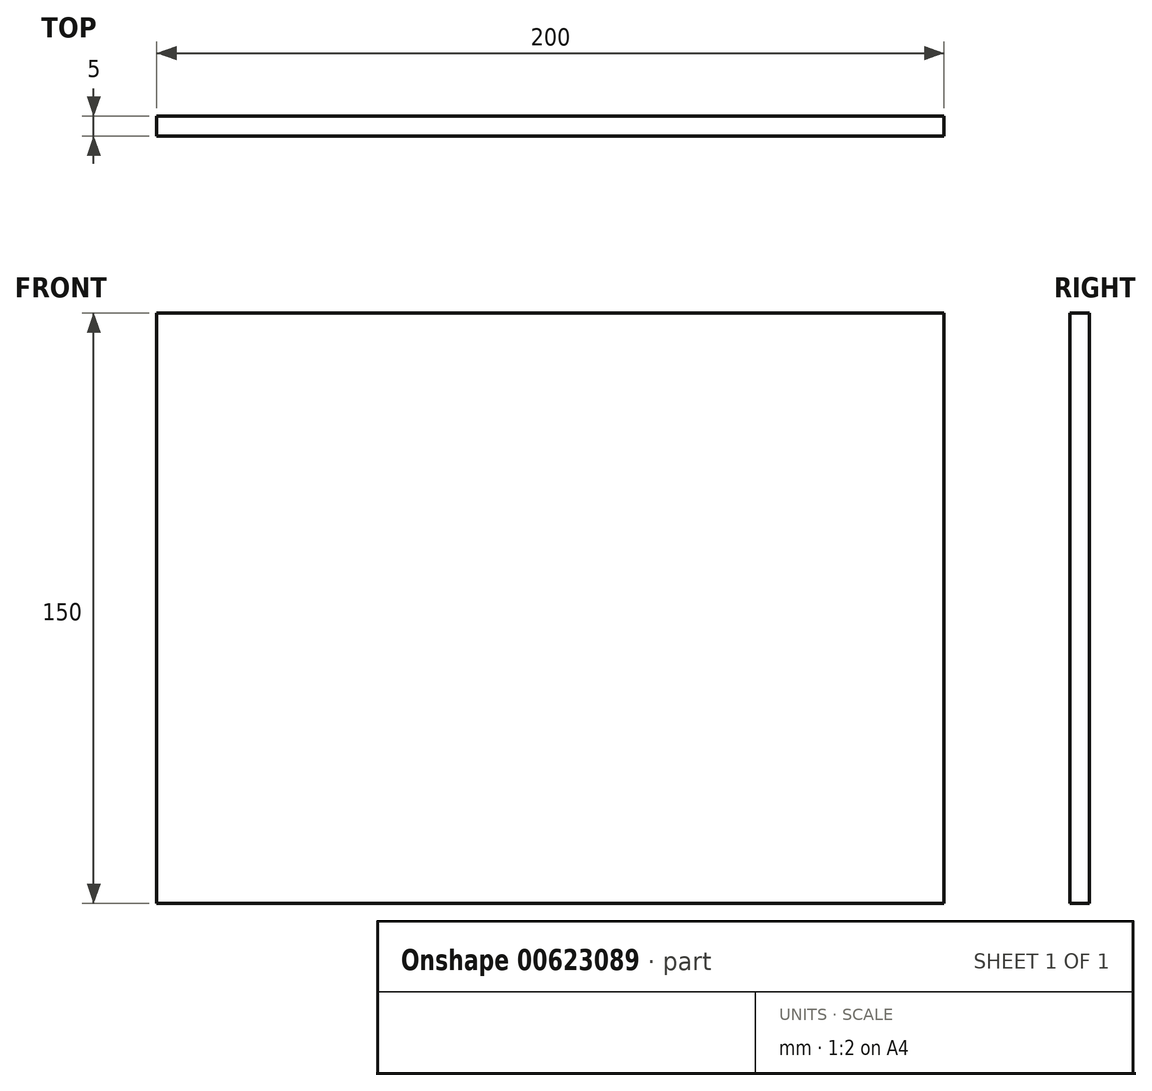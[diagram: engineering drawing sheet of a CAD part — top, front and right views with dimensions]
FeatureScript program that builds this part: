
annotation { "Feature Type Name" : "Feature", "Feature Type Description" : "" }
export const myFeature = defineFeature(function(context is Context, id is Id, definition is map)
    precondition{}
    {
        {
            var Q0;
            Q0=qCreatedBy(makeId("Front.planeOp"),FACE);
            var sketch = newSketch(context, id + "F0", { "sketchPlane" : qUnion([Q0])});
            skLineSegment(sketch, "E0.bottom", {"start": v(-200, 150) * mm, "end": v(0, 150) * mm});
            skLineSegment(sketch, "E0.top", {"start": v(-200, 0) * mm, "end": v(0, 0) * mm});
            skLineSegment(sketch, "E0.left", {"start": v(-200, 150) * mm, "end": v(-200, 0) * mm});
            skLineSegment(sketch, "E0.right", {"start": v(0, 150) * mm, "end": v(0, 0) * mm});
            skSolve(sketch);
        }
        {
            var Q0;
            Q0 = qSketchRegion(id + "F0", true);
            extrude(context, id + "F1", {"entities" : qUnion([Q0]), "depth" : 5 * mm, "offsetDistance" : 25 * mm});
        }
    });
